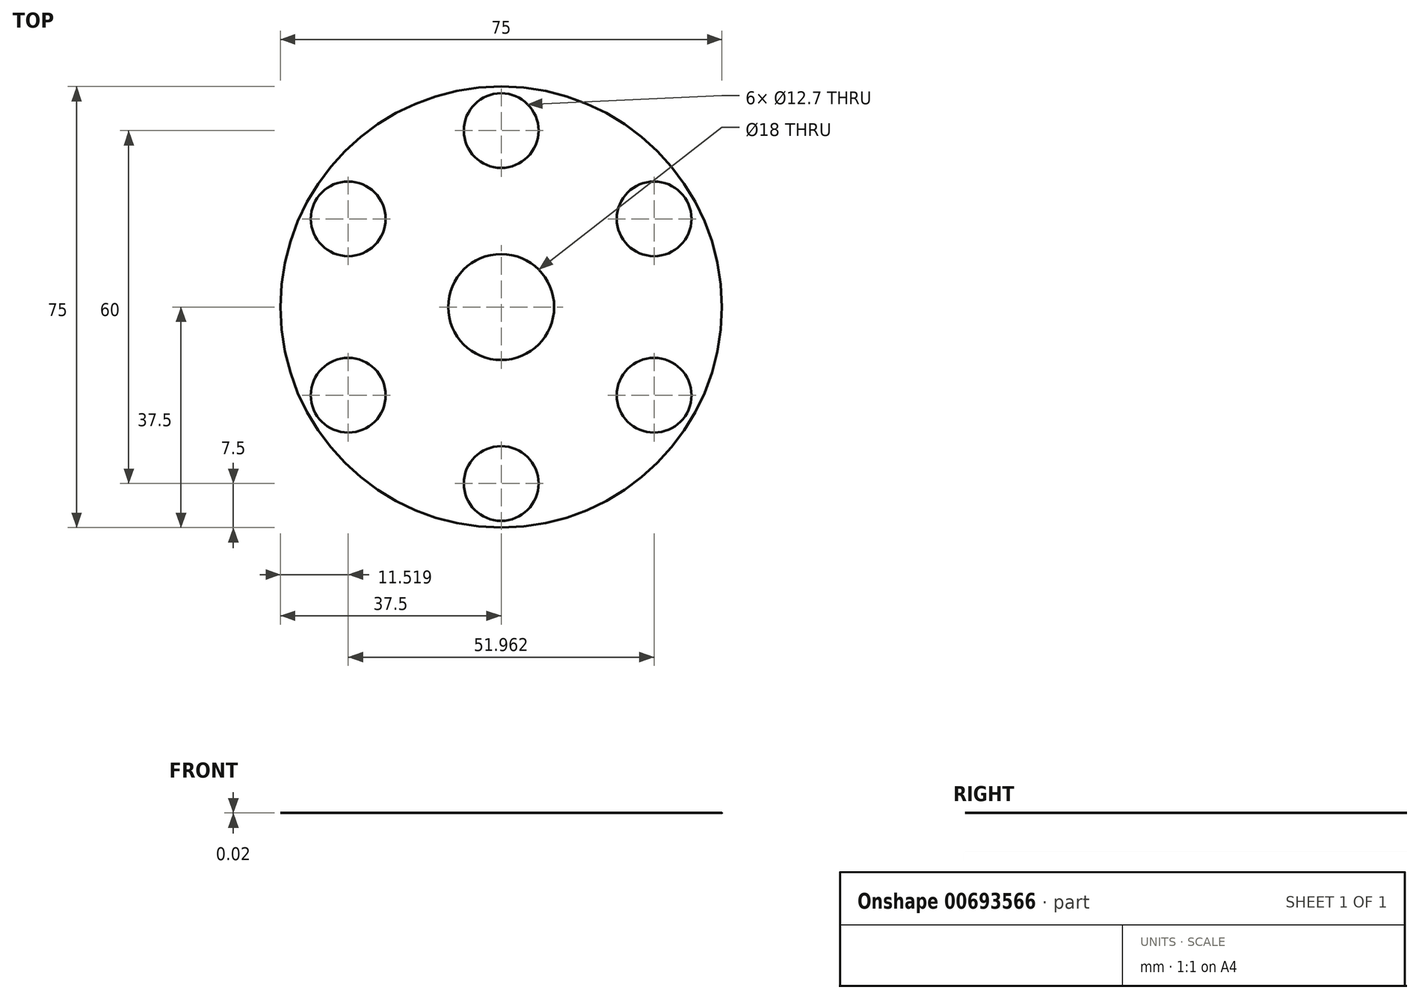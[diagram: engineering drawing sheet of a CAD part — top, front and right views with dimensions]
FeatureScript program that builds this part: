
annotation { "Feature Type Name" : "Feature", "Feature Type Description" : "" }
export const myFeature = defineFeature(function(context is Context, id is Id, definition is map)
    precondition{}
    {
        {
            var Q0;
            Q0=qCreatedBy(makeId("Top.planeOp"),FACE);
            var sketch = newSketch(context, id + "F0", { "sketchPlane" : qUnion([Q0])});
            skCircle(sketch, "E0", {"center": v(0, 0) * mm, "radius": 37.5 * mm});
            skSolve(sketch);
        }
        {
            var Q0;
            Q0=qSketchRegion(id+"F0",true);
            extrude(context, id + "F1", {"entities" : qUnion([Q0]), "depth" : 1 / 50.8 * mm, "offsetDistance" : 25 * mm});
        }
        {
            var Q0;
            Q0=makeQuery(id+"F1.opExtrude","CAP_FACE",FACE,{"disambiguationData":[OSD([sQuery(id+"F0.wireOp",EDGE,"E0")])],"isStart":false});
            var sketch = newSketch(context, id + "F2", { "sketchPlane" : qUnion([Q0])});
            skPoint(sketch, "E1", {"position": v(0, 0) * mm});
            skSolve(sketch);
        }
        {
            var Q0;
            Q0=sQuery(id+"F2.wireOp",VERTEX,"E1");
            var Q1;
            Q1=makeQuery(id+"F1.opExtrude","SWEPT_BODY",BODY,{"disambiguationData":[OSD([sQuery(id+"F0.wireOp",EDGE,"E0")])]});
            hole(context, id + "F3", {"style" : HoleStyle.SIMPLE, "endStyle" : HoleEndStyle.THROUGH, "holeDiameter" : 18 * mm, "majorDiameter" : 5 * mm, "isTappedThrough" : true, "tappedDepth" : 12 * mm, "tapClearance" : 3, "startFromSketch" : true, "locations" : qUnion([Q0]), "scope" : qUnion([Q1])});
        }
        {
            var Q0;
            Q0=makeQuery(id+"F1.opExtrude","CAP_FACE",FACE,{"disambiguationData":[OSD([sQuery(id+"F0.wireOp",EDGE,"E0")])],"isStart":false});
            var sketch = newSketch(context, id + "F4", { "sketchPlane" : qUnion([Q0])});
            skCircle(sketch, "E2.cCircle", {"center": v(0, 0) * mm, "radius": 25.98 * mm, "construction": true});
            skLineSegment(sketch, "E2.0", {"start": v(25.98, -15) * mm, "end": v(0, -30) * mm, "construction": true});
            skLineSegment(sketch, "E2.1", {"start": v(0, -30) * mm, "end": v(-25.98, -15) * mm, "construction": true});
            skLineSegment(sketch, "E2.2", {"start": v(-25.98, -15) * mm, "end": v(-25.98, 15) * mm, "construction": true});
            skLineSegment(sketch, "E2.3", {"start": v(-25.98, 15) * mm, "end": v(0, 30) * mm, "construction": true});
            skLineSegment(sketch, "E2.4", {"start": v(0, 30) * mm, "end": v(25.98, 15) * mm, "construction": true});
            skLineSegment(sketch, "E2.5", {"start": v(25.98, 15) * mm, "end": v(25.98, -15) * mm, "construction": true});
            skPoint(sketch, "E2.0.midPoint", {"position": v(13, -22.5) * mm});
            skSolve(sketch);
        }
        {
            var Q0;
            Q0=sQuery(id+"F4.wireOp",VERTEX,"E2.4.start");
            var Q1;
            Q1=sQuery(id+"F4.wireOp",VERTEX,"E2.5.start");
            var Q2;
            Q2=sQuery(id+"F4.wireOp",VERTEX,"E2.5.end");
            var Q3;
            Q3=sQuery(id+"F4.wireOp",VERTEX,"E2.0.end");
            var Q4;
            Q4=sQuery(id+"F4.wireOp",VERTEX,"E2.2.start");
            var Q5;
            Q5=sQuery(id+"F4.wireOp",VERTEX,"E2.3.start");
            var Q6;
            Q6=makeQuery(id+"F1.opExtrude","SWEPT_BODY",BODY,{"disambiguationData":[OSD([sQuery(id+"F0.wireOp",EDGE,"E0")])]});
            hole(context, id + "F5", {"style" : HoleStyle.C_BORE, "endStyle" : HoleEndStyle.THROUGH, "holeDiameter" : 6.5 * mm, "cBoreDiameter" : 12.7 * mm, "cBoreDepth" : 10 * mm, "majorDiameter" : 5 * mm, "isTappedThrough" : true, "tappedDepth" : 12 * mm, "tapClearance" : 3, "startFromSketch" : true, "locations" : qUnion([Q0, Q1, Q2, Q3, Q4, Q5]), "scope" : qUnion([Q6])});
        }
    });
